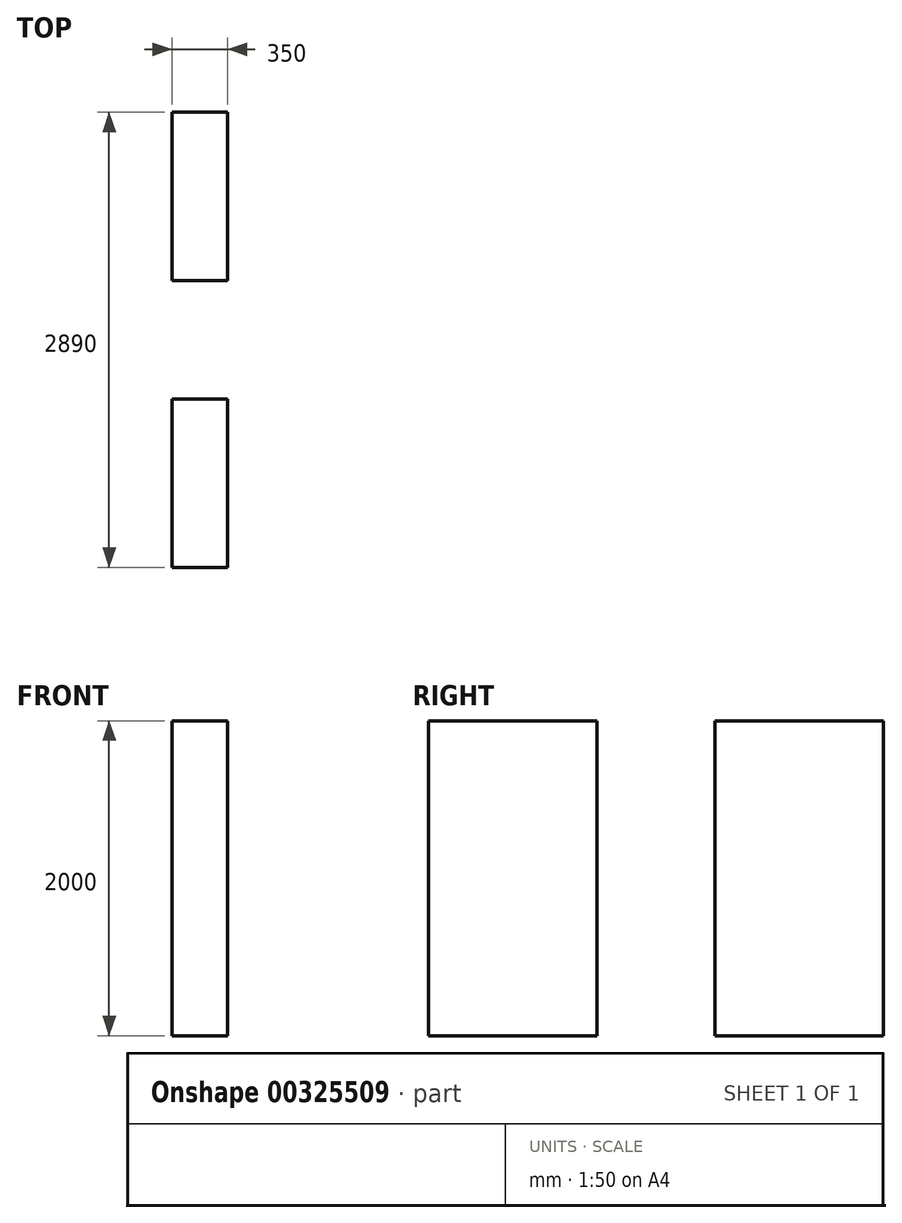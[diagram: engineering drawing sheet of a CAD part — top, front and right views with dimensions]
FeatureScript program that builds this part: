
annotation { "Feature Type Name" : "Feature", "Feature Type Description" : "" }
export const myFeature = defineFeature(function(context is Context, id is Id, definition is map)
    precondition{}
    {
        {
            var Q0;
            Q0=qCreatedBy(makeId("Top.planeOp"),FACE);
            var sketch = newSketch(context, id + "F0", { "sketchPlane" : qUnion([Q0])});
            skLineSegment(sketch, "E0.bottom", {"start": v(-175, 375) * mm, "end": v(-175, 1445) * mm});
            skLineSegment(sketch, "E0.top", {"start": v(175, 375) * mm, "end": v(175, 1445) * mm});
            skLineSegment(sketch, "E0.left", {"start": v(-175, 375) * mm, "end": v(175, 375) * mm});
            skLineSegment(sketch, "E0.right", {"start": v(-175, 1445) * mm, "end": v(175, 1445) * mm});
            skPoint(sketch, "E0.middle", {"position": v(0, 910) * mm});
            skLineSegment(sketch, "E1.bottom", {"start": v(-175, -1445) * mm, "end": v(-175, -375) * mm});
            skLineSegment(sketch, "E1.top", {"start": v(175, -1445) * mm, "end": v(175, -375) * mm});
            skLineSegment(sketch, "E1.left", {"start": v(-175, -1445) * mm, "end": v(175, -1445) * mm});
            skLineSegment(sketch, "E1.right", {"start": v(-175, -375) * mm, "end": v(175, -375) * mm});
            skPoint(sketch, "E1.middle", {"position": v(0, -910) * mm});
            skLineSegment(sketch, "E2", {"start": v(0, 375) * mm, "end": v(0, -375) * mm, "construction": true});
            skSolve(sketch);
        }
        {
            var Q0;
            Q0 = qSketchRegion(id + "F0", true);
            extrude(context, id + "F1", {"entities" : qUnion([Q0]), "depth" : 2000 * mm});
        }
    });
